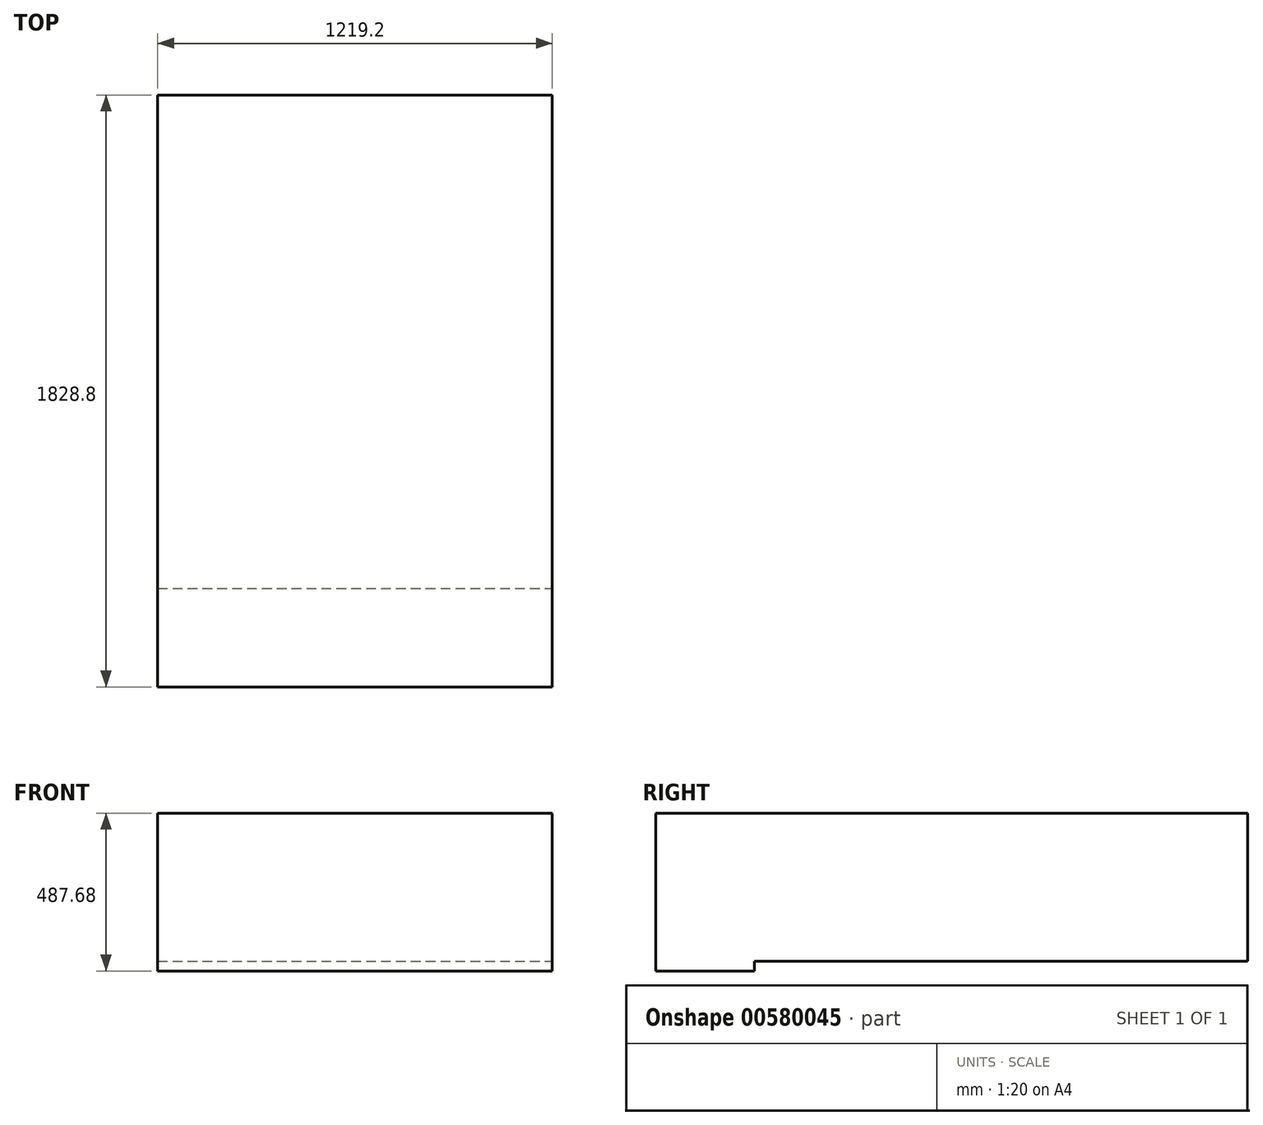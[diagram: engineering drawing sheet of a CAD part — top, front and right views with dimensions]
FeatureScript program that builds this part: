
annotation { "Feature Type Name" : "Feature", "Feature Type Description" : "" }
export const myFeature = defineFeature(function(context is Context, id is Id, definition is map)
    precondition{}
    {
        {
            var Q0;
            Q0=qCreatedBy(makeId("Top.planeOp"),FACE);
            var sketch = newSketch(context, id + "F0", { "sketchPlane" : qUnion([Q0])});
            skLineSegment(sketch, "E0.bottom", {"start": v(-990.76, -928.03) * mm, "end": v(228.44, -928.03) * mm});
            skLineSegment(sketch, "E0.top", {"start": v(-990.76, 900.77) * mm, "end": v(228.44, 900.77) * mm});
            skLineSegment(sketch, "E0.left", {"start": v(-990.76, -928.03) * mm, "end": v(-990.76, 900.77) * mm});
            skLineSegment(sketch, "E0.right", {"start": v(228.44, -928.03) * mm, "end": v(228.44, 900.77) * mm});
            skSolve(sketch);
        }
        {
            var Q0;
            Q0 = qSketchRegion(id + "F0", true);
            extrude(context, id + "F1", {"entities" : qUnion([Q0]), "depth" : 457.2 * mm, "offsetDistance" : 30.48 * mm});
        }
        {
            var Q0;
            Q0=makeQuery(id+"F1.opExtrude","CAP_FACE",FACE,{"disambiguationData":[OSD([sQuery(id+"F0.wireOp",EDGE,"E0.bottom"),sQuery(id+"F0.wireOp",EDGE,"E0.top"),sQuery(id+"F0.wireOp",EDGE,"E0.left"),sQuery(id+"F0.wireOp",EDGE,"E0.right")])],"isStart":true});
            var sketch = newSketch(context, id + "F2", { "sketchPlane" : qUnion([Q0])});
            skLineSegment(sketch, "E1.bottom", {"start": v(-990.76, 928.03) * mm, "end": v(-381.16, 928.03) * mm});
            skLineSegment(sketch, "E1.top", {"start": v(-990.76, 623.23) * mm, "end": v(-381.16, 623.23) * mm});
            skLineSegment(sketch, "E1.left", {"start": v(-990.76, 928.03) * mm, "end": v(-990.76, 623.23) * mm});
            skLineSegment(sketch, "E1.right", {"start": v(-381.16, 928.03) * mm, "end": v(-381.16, 623.23) * mm});
            skLineSegment(sketch, "E2.bottom", {"start": v(-381.16, 928.03) * mm, "end": v(228.44, 928.03) * mm});
            skLineSegment(sketch, "E2.top", {"start": v(-381.16, 623.23) * mm, "end": v(228.44, 623.23) * mm});
            skLineSegment(sketch, "E2.right", {"start": v(228.44, 928.03) * mm, "end": v(228.44, 623.23) * mm});
            skSolve(sketch);
        }
        {
            var Q0;
            Q0 = qSketchRegion(id + "F2", true);
            extrude(context, id + "F3", {"entities" : qUnion([Q0]), "operationType" : NewBodyOperationType.ADD, "depth" : 30.48 * mm, "offsetDistance" : 30.48 * mm});
        }
    });
